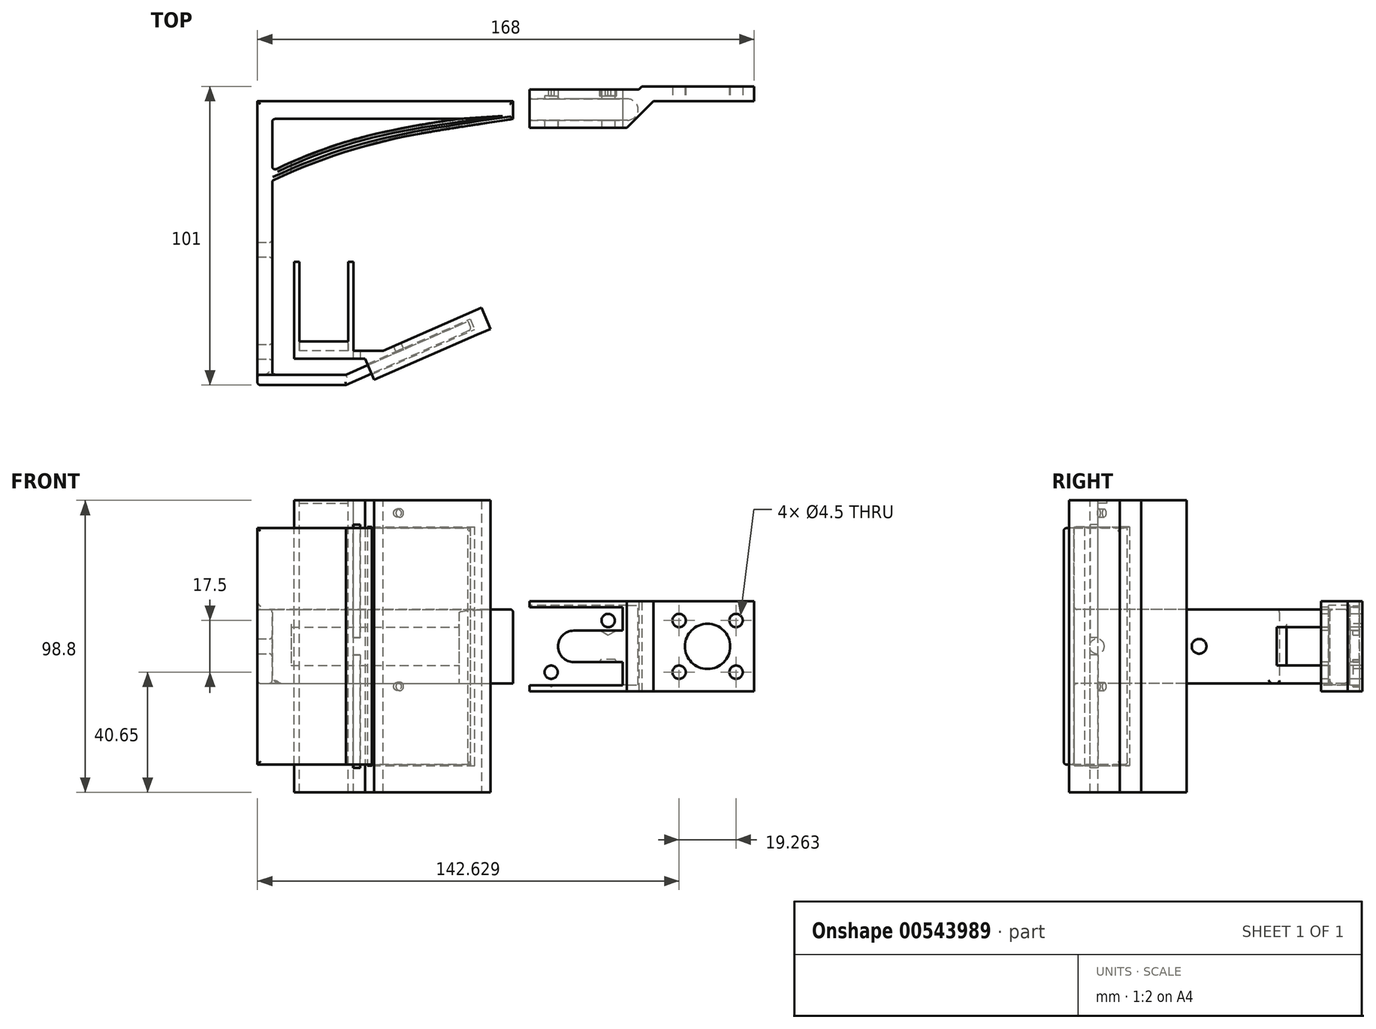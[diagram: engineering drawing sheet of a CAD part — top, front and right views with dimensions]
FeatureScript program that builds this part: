
annotation { "Feature Type Name" : "Feature", "Feature Type Description" : "" }
export const myFeature = defineFeature(function(context is Context, id is Id, definition is map)
    precondition{}
    {
        {
            var Q0;
            Q0=qCreatedBy(makeId("Top.planeOp"),FACE);
            var sketch = newSketch(context, id + "F0", { "sketchPlane" : qUnion([Q0])});
            skLineSegment(sketch, "E0.bottom", {"start": v(-68.2, 34.46) * mm, "end": v(54.8, 34.46) * mm});
            skLineSegment(sketch, "E0.left", {"start": v(-68.2, 34.46) * mm, "end": v(-68.2, 28.46) * mm});
            skLineSegment(sketch, "E1.bottom", {"start": v(-68.2, 28.46) * mm, "end": v(-63.2, 28.46) * mm});
            skLineSegment(sketch, "E1.top", {"start": v(-68.2, -61.54) * mm, "end": v(-63.2, -61.54) * mm});
            skLineSegment(sketch, "E1.left", {"start": v(-68.2, 28.46) * mm, "end": v(-68.2, -61.54) * mm});
            skLineSegment(sketch, "E2", {"start": v(-63.2, 7.6) * mm, "end": v(-63.2, -61.54) * mm});
            skLineSegment(sketch, "E3", {"start": v(-63.2, 28.46) * mm, "end": v(-63.2, 10.83) * mm});
            skFitSpline(sketch, "E4", {"points": [v(-63.2, 10.83) * mm, v(-36.5, 21.22) * mm, v(0, 28.46) * mm], "startDerivative": vector(52.11, 25.6) * mm, "endDerivative": vector(73.7, 10.1) * mm});
            skFitSpline(sketch, "E5", {"points": [v(-63.2, 7.6) * mm, v(-25.3, 20.96) * mm, v(18.24, 28.46) * mm], "startDerivative": vector(89.55, 42.22) * mm, "endDerivative": vector(130.6, 19.81) * mm});
            skLineSegment(sketch, "E6", {"start": v(54.8, 34.46) * mm, "end": v(54.8, 32.96) * mm});
            skLineSegment(sketch, "E7", {"start": v(54.8, 29.96) * mm, "end": v(54.8, 28.46) * mm});
            skLineSegment(sketch, "E8", {"start": v(18.24, 28.46) * mm, "end": v(54.8, 28.46) * mm});
            skLineSegment(sketch, "E9", {"start": v(-63.2, 28.46) * mm, "end": v(0, 28.46) * mm});
            skLineSegment(sketch, "E10", {"start": v(54.8, 32.96) * mm, "end": v(54.8, 29.96) * mm});
            skSolve(sketch);
        }
        {
            var Q0;
            Q0=makeQuery(id+"F0.imprint","IMPRINT",FACE,{"disambiguationData":[TD([[makeQuery(id+"F0.imprint","IMPRINT",EDGE,{"derivedFrom":sQuery(id+"F0.wireOp",EDGE,"E0.bottom")}),-1.0]])]});
            extrude(context, id + "F1", {"entities" : qUnion([Q0]), "depth" : 25 * mm, "offsetDistance" : 25 * mm});
        }
        {
            var Q0;
            Q0=makeQuery(id+"F1.opExtrude","SWEPT_FACE",FACE,{"disambiguationData":[OSD([sQuery(id+"F0.wireOp",EDGE,"E2")])]});
            var sketch = newSketch(context, id + "F2", { "sketchPlane" : qUnion([Q0])});
            skCircle(sketch, "E11", {"center": v(-50.3, 12.5) * mm, "radius": 2.5 * mm});
            skCircle(sketch, "E12", {"center": v(-15.75, 12.5) * mm, "radius": 2.5 * mm});
            skSolve(sketch);
        }
        {
            var Q0;
            Q0=makeQuery(id+"F2.imprint","IMPRINT",FACE,{"disambiguationData":[TD([[makeQuery(id+"F2.imprint","IMPRINT",EDGE,{"derivedFrom":sQuery(id+"F2.wireOp",EDGE,"E12")}),1.0]])]});
            var Q1;
            Q1=makeQuery(id+"F2.imprint","IMPRINT",FACE,{"disambiguationData":[TD([[makeQuery(id+"F2.imprint","IMPRINT",EDGE,{"derivedFrom":sQuery(id+"F2.wireOp",EDGE,"E11")}),1.0]])]});
            extrude(context, id + "F3", {"entities" : qUnion([Q0, Q1]), "operationType" : NewBodyOperationType.REMOVE, "endBound" : BoundingType.THROUGH_ALL, "oppositeDirection" : true, "depth" : 25 * mm, "offsetDistance" : 25 * mm});
        }
        {
            var Q0;
            Q0=makeQuery(id+"F1.opExtrude","SWEPT_FACE",FACE,{"disambiguationData":[OSD([sQuery(id+"F0.wireOp",EDGE,"E9")])]});
            var sketch = newSketch(context, id + "F4", { "sketchPlane" : qUnion([Q0])});
            skLineSegment(sketch, "E13.bottom", {"start": v(0, 6.04) * mm, "end": v(-56.85, 6.04) * mm});
            skLineSegment(sketch, "E13.top", {"start": v(0, 18.96) * mm, "end": v(-56.85, 18.96) * mm});
            skLineSegment(sketch, "E13.left", {"start": v(0, 6.04) * mm, "end": v(0, 18.96) * mm});
            skLineSegment(sketch, "E13.right", {"start": v(-56.85, 6.04) * mm, "end": v(-56.85, 18.96) * mm});
            skLineSegment(sketch, "E14.0", {"start": v(-63.2, 25) * mm, "end": v(0, 25) * mm});
            skLineSegment(sketch, "E15.0", {"start": v(-63.2, 0) * mm, "end": v(0, 0) * mm});
            skLineSegment(sketch, "E16", {"start": v(0, 25) * mm, "end": v(0, 18.96) * mm});
            skLineSegment(sketch, "E17", {"start": v(0, 6.04) * mm, "end": v(0, 0) * mm});
            skSolve(sketch);
        }
        {
            var Q0;
            Q0=makeQuery(id+"F4.imprint","IMPRINT",FACE,{"disambiguationData":[TD([[makeQuery(id+"F4.imprint","IMPRINT",EDGE,{"derivedFrom":sQuery(id+"F4.wireOp",EDGE,"E13.bottom")}),-1.0]])]});
            extrude(context, id + "F5", {"entities" : qUnion([Q0]), "operationType" : NewBodyOperationType.REMOVE, "endBound" : BoundingType.THROUGH_ALL, "depth" : 25 * mm, "offsetDistance" : 25 * mm});
        }
        {
            var Q0;
            Q0=makeQuery(id+"F1.opExtrude","SWEPT_FACE",FACE,{"disambiguationData":[OSD([sQuery(id+"F0.wireOp",EDGE,"E8")])]});
            var sketch = newSketch(context, id + "F6", { "sketchPlane" : qUnion([Q0])});
            skLineSegment(sketch, "E18", {"start": v(54.8, 25) * mm, "end": v(54.8, 18.5) * mm});
            skLineSegment(sketch, "E19", {"start": v(54.8, 18.5) * mm, "end": v(54.8, 6.5) * mm});
            skLineSegment(sketch, "E20", {"start": v(54.8, 6.5) * mm, "end": v(54.8, 0) * mm});
            skLineSegment(sketch, "E21", {"start": v(54.8, 18.5) * mm, "end": v(38.8, 18.5) * mm});
            skLineSegment(sketch, "E22", {"start": v(32.8, 12.5) * mm, "end": v(32.8, 12.5) * mm});
            skLineSegment(sketch, "E23", {"start": v(38.8, 6.5) * mm, "end": v(54.8, 6.5) * mm});
            skPoint(sketch, "E24.visualSharp", {"position": v(32.8, 18.5) * mm});
            skArc(sketch, "E24.filletArc", {"start": v(38.8, 18.5) * mm, "mid": v(34.55, 16.74) * mm, "end": v(32.8, 12.5) * mm});
            skPoint(sketch, "E25.visualSharp", {"position": v(32.8, 6.5) * mm});
            skArc(sketch, "E25.filletArc", {"start": v(32.8, 12.5) * mm, "mid": v(34.55, 8.26) * mm, "end": v(38.8, 6.5) * mm});
            skCircle(sketch, "E26", {"center": v(31.16, 21.25) * mm, "radius": 2.25 * mm});
            skCircle(sketch, "E27.MirrorC", {"center": v(31.16, 3.75) * mm, "radius": 2.25 * mm});
            skCircle(sketch, "E28.MirrorC", {"center": v(50.42, 21.25) * mm, "radius": 2.25 * mm});
            skCircle(sketch, "E29.MirrorC", {"center": v(50.42, 3.75) * mm, "radius": 2.25 * mm});
            skSolve(sketch);
        }
        {
            var Q0;
            Q0=makeQuery(id+"F6.imprint","IMPRINT",FACE,{"disambiguationData":[TD([[makeQuery(id+"F6.imprint","IMPRINT",EDGE,{"derivedFrom":sQuery(id+"F6.wireOp",EDGE,"E26")}),1.0]])]});
            var Q1;
            Q1=makeQuery(id+"F6.imprint","IMPRINT",FACE,{"disambiguationData":[TD([[makeQuery(id+"F6.imprint","IMPRINT",EDGE,{"derivedFrom":sQuery(id+"F6.wireOp",EDGE,"E28.MirrorC")}),-1.0]])]});
            var Q2;
            Q2=makeQuery(id+"F6.imprint","IMPRINT",FACE,{"disambiguationData":[TD([[makeQuery(id+"F6.imprint","IMPRINT",EDGE,{"derivedFrom":sQuery(id+"F6.wireOp",EDGE,"E19")}),-1.0]])]});
            var Q3;
            Q3=makeQuery(id+"F6.imprint","IMPRINT",FACE,{"disambiguationData":[TD([[makeQuery(id+"F6.imprint","IMPRINT",EDGE,{"derivedFrom":sQuery(id+"F6.wireOp",EDGE,"E29.MirrorC")}),1.0]])]});
            var Q4;
            Q4=makeQuery(id+"F6.imprint","IMPRINT",FACE,{"disambiguationData":[TD([[makeQuery(id+"F6.imprint","IMPRINT",EDGE,{"derivedFrom":sQuery(id+"F6.wireOp",EDGE,"E27.MirrorC")}),-1.0]])]});
            extrude(context, id + "F7", {"entities" : qUnion([Q0, Q1, Q2, Q3, Q4]), "operationType" : NewBodyOperationType.REMOVE, "oppositeDirection" : true, "depth" : 25 * mm, "offsetDistance" : 25 * mm});
        }
        {
            var Q0;
            Q0=makeQuery(id+"F1.opExtrude","SWEPT_FACE",FACE,{"disambiguationData":[OSD([sQuery(id+"F0.wireOp",EDGE,"E1.top")])]});
            var sketch = newSketch(context, id + "F8", { "sketchPlane" : qUnion([Q0])});
            skLineSegment(sketch, "E30.bottom", {"start": v(-68.2, 12.5) * mm, "end": v(-38.2, 12.5) * mm});
            skLineSegment(sketch, "E30.top", {"start": v(-68.2, -27.5) * mm, "end": v(-38.2, -27.5) * mm});
            skLineSegment(sketch, "E30.left", {"start": v(-68.2, 12.5) * mm, "end": v(-68.2, -27.5) * mm});
            skLineSegment(sketch, "E30.right", {"start": v(-38.2, 12.5) * mm, "end": v(-38.2, -27.5) * mm});
            skLineSegment(sketch, "E31.top", {"start": v(-68.2, 52.5) * mm, "end": v(-38.2, 52.5) * mm});
            skLineSegment(sketch, "E31.left", {"start": v(-68.2, 12.5) * mm, "end": v(-68.2, 52.5) * mm});
            skLineSegment(sketch, "E31.right", {"start": v(-38.2, 12.5) * mm, "end": v(-38.2, 52.5) * mm});
            skSolve(sketch);
        }
        {
            var Q0;
            {var subQ4=sQuery(id+"F8.wireOp",EDGE,"E31.top");Q0=makeQuery(id+"F8.imprint","IMPRINT",FACE,{"disambiguationData":[TD([[makeQuery(id+"F8.imprint","IMPRINT",EDGE,{"derivedFrom":subQ4}),-1.0]])]});}
            var Q1;
            {var subQ4=sQuery(id+"F8.wireOp",EDGE,"E30.top");Q1=makeQuery(id+"F8.imprint","IMPRINT",FACE,{"disambiguationData":[TD([[makeQuery(id+"F8.imprint","IMPRINT",EDGE,{"derivedFrom":subQ4}),1.0]])]});}
            extrude(context, id + "F9", {"entities" : qUnion([Q0, Q1]), "operationType" : NewBodyOperationType.ADD, "oppositeDirection" : true, "depth" : 3.5 * mm, "offsetDistance" : 25 * mm});
        }
        {
            var Q0;
            Q0=makeQuery(id+"F9.opExtrude","SWEPT_FACE",FACE,{"disambiguationData":[OSD([sQuery(id+"F8.wireOp",EDGE,"E31.top")])]});
            var sketch = newSketch(context, id + "F10", { "sketchPlane" : qUnion([Q0])});
            skLineSegment(sketch, "E32", {"start": v(-38.2, -58.04) * mm, "end": v(3.02, -40) * mm});
            skLineSegment(sketch, "E33", {"start": v(3.02, -40) * mm, "end": v(4.22, -42.75) * mm});
            skLineSegment(sketch, "E34", {"start": v(4.22, -42.75) * mm, "end": v(-38.2, -61.54) * mm});
            skSolve(sketch);
        }
        {
            var Q0;
            Q0=makeQuery(id+"F10.imprint","IMPRINT",FACE,{"disambiguationData":[TD([[makeQuery(id+"F10.imprint","IMPRINT",EDGE,{"derivedFrom":sQuery(id+"F10.wireOp",EDGE,"E32")}),-1.0]])]});
            extrude(context, id + "F11", {"entities" : qUnion([Q0]), "operationType" : NewBodyOperationType.ADD, "oppositeDirection" : true, "depth" : 80 * mm, "offsetDistance" : 25 * mm});
        }
        {
            var Q0;
            Q0=makeQuery(id+"F1.opExtrude","CAP_EDGE",EDGE,{"disambiguationData":[OSD([sQuery(id+"F0.wireOp",EDGE,"E0.bottom")])],"isStart":false});
            var Q1;
            Q1=makeQuery(id+"F1.opExtrude","CAP_EDGE",EDGE,{"disambiguationData":[OSD([sQuery(id+"F0.wireOp",EDGE,"E0.bottom")])],"isStart":true});
            var Q2;
            {var subQ0=sQuery(id+"F0.wireOp",EDGE,"E0.bottom");var subQ3=sQuery(id+"F0.wireOp",EDGE,"E6");Q2=makeQuery(id+"F7.boolean.opBoolean","SPLIT",EDGE,{"disambiguationData":[TD([makeQuery(id+"F7.opExtrude","SWEPT_FACE",FACE,{"disambiguationData":[OSD([sQuery(id+"F6.wireOp",EDGE,"E21")])]})])],"derivedFrom":makeQuery(id+"F1.opExtrude","SWEPT_EDGE",EDGE,{"disambiguationData":[OSD([subQ0,subQ3])]})});}
            var Q3;
            {var subQ2=sQuery(id+"F0.wireOp",EDGE,"E10");var subQ3=sQuery(id+"F0.wireOp",EDGE,"E7");var subQ4=sQuery(id+"F0.wireOp",EDGE,"E6");Q3=makeQuery(id+"F7.boolean.opBoolean","SPLIT",FACE,{"disambiguationData":[TD([makeQuery(id+"F7.opExtrude","SWEPT_FACE",FACE,{"disambiguationData":[OSD([sQuery(id+"F6.wireOp",EDGE,"E21")])]})])],"derivedFrom":makeQuery(id+"F1.opExtrude","SWEPT_FACE",FACE,{"disambiguationData":[OSD([subQ4,subQ3,subQ2])]})});}
            var Q4;
            Q4=makeQuery(id+"F7.boolean.opBoolean","COPY",EDGE,{"derivedFrom":makeQuery(id+"F7.opExtrude","SWEPT_EDGE",EDGE,{"disambiguationData":[OSD([sQuery(id+"F6.wireOp",EDGE,"E18"),sQuery(id+"F6.wireOp",EDGE,"E19"),sQuery(id+"F6.wireOp",EDGE,"E21")])]})});
            var Q5;
            Q5=makeQuery(id+"F7.boolean.opBoolean","COPY",EDGE,{"derivedFrom":makeQuery(id+"F7.opExtrude","SWEPT_EDGE",EDGE,{"disambiguationData":[OSD([sQuery(id+"F6.wireOp",EDGE,"E19"),sQuery(id+"F6.wireOp",EDGE,"E20"),sQuery(id+"F6.wireOp",EDGE,"E23")])]})});
            var Q6;
            Q6=makeQuery(id+"F7.boolean.opBoolean","INTERSECT",EDGE,{"derivedFrom":[makeQuery(id+"F1.opExtrude","SWEPT_FACE",FACE,{"disambiguationData":[OSD([sQuery(id+"F0.wireOp",EDGE,"E0.bottom")])]}),makeQuery(id+"F7.opExtrude","SWEPT_FACE",FACE,{"disambiguationData":[OSD([sQuery(id+"F6.wireOp",EDGE,"E23")])]})]});
            var Q7;
            Q7=makeQuery(id+"F7.boolean.opBoolean","INTERSECT",EDGE,{"derivedFrom":[makeQuery(id+"F1.opExtrude","SWEPT_FACE",FACE,{"disambiguationData":[OSD([sQuery(id+"F0.wireOp",EDGE,"E0.bottom")])]}),makeQuery(id+"F7.opExtrude","SWEPT_FACE",FACE,{"disambiguationData":[OSD([sQuery(id+"F6.wireOp",EDGE,"E24.filletArc"),sQuery(id+"F6.wireOp",EDGE,"E25.filletArc")])]})]});
            var Q8;
            {var subQ1=sQuery(id+"F0.wireOp",EDGE,"E8");var subQ2=sQuery(id+"F0.wireOp",EDGE,"E7");Q8=makeQuery(id+"F7.boolean.opBoolean","SPLIT",EDGE,{"disambiguationData":[TD([makeQuery(id+"F7.opExtrude","SWEPT_FACE",FACE,{"disambiguationData":[OSD([sQuery(id+"F6.wireOp",EDGE,"E23")])]})])],"derivedFrom":makeQuery(id+"F1.opExtrude","SWEPT_EDGE",EDGE,{"disambiguationData":[OSD([subQ2,subQ1])]})});}
            var Q9;
            Q9=makeQuery(id+"F1.opExtrude","CAP_EDGE",EDGE,{"disambiguationData":[OSD([sQuery(id+"F0.wireOp",EDGE,"E8")])],"isStart":true});
            var Q10;
            Q10=makeQuery(id+"F1.opExtrude","SWEPT_FACE",FACE,{"disambiguationData":[OSD([sQuery(id+"F0.wireOp",EDGE,"E2")])]});
            var Q11;
            Q11=makeQuery(id+"F1.opExtrude","CAP_EDGE",EDGE,{"disambiguationData":[OSD([sQuery(id+"F0.wireOp",EDGE,"E0.left"),sQuery(id+"F0.wireOp",EDGE,"E1.left")])],"isStart":true});
            var Q12;
            Q12=makeQuery(id+"F1.opExtrude","SWEPT_FACE",FACE,{"disambiguationData":[OSD([sQuery(id+"F0.wireOp",EDGE,"E3")])]});
            var Q13;
            Q13=makeQuery(id+"F11.opExtrude","CAP_EDGE",EDGE,{"disambiguationData":[OSD([sQuery(id+"F10.wireOp",EDGE,"E32")])],"isStart":false});
            var Q14;
            Q14=makeQuery(id+"F11.opExtrude","CAP_EDGE",EDGE,{"disambiguationData":[OSD([sQuery(id+"F10.wireOp",EDGE,"E34")])],"isStart":false});
            var Q15;
            Q15=makeQuery(id+"F9.opExtrude","CAP_EDGE",EDGE,{"disambiguationData":[OSD([sQuery(id+"F8.wireOp",EDGE,"E30.top")])],"isStart":false});
            var Q16;
            Q16=makeQuery(id+"F9.opExtrude","CAP_EDGE",EDGE,{"disambiguationData":[OSD([sQuery(id+"F8.wireOp",EDGE,"E30.top")])],"isStart":true});
            var Q17;
            Q17=makeQuery(id+"F11.opExtrude","SWEPT_EDGE",EDGE,{"disambiguationData":[OSD([sQuery(id+"F10.wireOp",EDGE,"E33"),sQuery(id+"F10.wireOp",EDGE,"E34")])]});
            var Q18;
            Q18=makeQuery(id+"F11.opExtrude","CAP_EDGE",EDGE,{"disambiguationData":[OSD([sQuery(id+"F10.wireOp",EDGE,"E34")])],"isStart":true});
            var Q19;
            Q19=makeQuery(id+"F9.opExtrude","CAP_EDGE",EDGE,{"disambiguationData":[OSD([sQuery(id+"F8.wireOp",EDGE,"E31.top")])],"isStart":true});
            var Q20;
            Q20=makeQuery(id+"F9.boolean.opBoolean","MERGE",EDGE,{"derivedFrom":[makeQuery(id+"F1.opExtrude","SWEPT_EDGE",EDGE,{"disambiguationData":[OSD([sQuery(id+"F0.wireOp",EDGE,"E1.top"),sQuery(id+"F0.wireOp",EDGE,"E1.left")])]}),makeQuery(id+"F9.opExtrude","CAP_EDGE",EDGE,{"disambiguationData":[OSD([sQuery(id+"F8.wireOp",EDGE,"E30.left")])],"isStart":true}),makeQuery(id+"F9.opExtrude","CAP_EDGE",EDGE,{"disambiguationData":[OSD([sQuery(id+"F8.wireOp",EDGE,"E31.left")])],"isStart":true})]});
            var Q21;
            Q21=makeQuery(id+"F1.opExtrude","CAP_FACE",FACE,{"disambiguationData":[OSD([sQuery(id+"F0.wireOp",EDGE,"E0.bottom"),sQuery(id+"F0.wireOp",EDGE,"E0.left"),sQuery(id+"F0.wireOp",EDGE,"E1.top"),sQuery(id+"F0.wireOp",EDGE,"E1.left"),sQuery(id+"F0.wireOp",EDGE,"E2"),sQuery(id+"F0.wireOp",EDGE,"E3"),sQuery(id+"F0.wireOp",EDGE,"E4"),sQuery(id+"F0.wireOp",EDGE,"E5"),sQuery(id+"F0.wireOp",EDGE,"E6"),sQuery(id+"F0.wireOp",EDGE,"E7"),sQuery(id+"F0.wireOp",EDGE,"E8"),sQuery(id+"F0.wireOp",EDGE,"E9"),sQuery(id+"F0.wireOp",EDGE,"E10")])],"isStart":false});
            var Q22;
            Q22=makeQuery(id+"F5.boolean.opBoolean","INTERSECT",EDGE,{"derivedFrom":[makeQuery(id+"F1.opExtrude","SWEPT_FACE",FACE,{"disambiguationData":[OSD([sQuery(id+"F0.wireOp",EDGE,"E4")])]}),makeQuery(id+"F5.opExtrude","SWEPT_FACE",FACE,{"disambiguationData":[OSD([sQuery(id+"F4.wireOp",EDGE,"E13.top")])]})]});
            fillet(context, id + "F12", {"entities" : qUnion([Q0, Q1, Q2, Q3, Q4, Q5, Q6, Q7, Q8, Q9, Q10, Q11, Q12, Q13, Q14, Q15, Q16, Q17, Q18, Q19, Q20, Q21, Q22]), "radius" : 1 * mm, "tangentPropagation" : true, "allowEdgeOverflow" : false});
        }
        {
            var Q0;
            Q0=makeQuery(id+"F1.opExtrude","SWEPT_FACE",FACE,{"disambiguationData":[OSD([sQuery(id+"F0.wireOp",EDGE,"E0.bottom")])]});
            var sketch = newSketch(context, id + "F13", { "sketchPlane" : qUnion([Q0])});
            skCircle(sketch, "E35.0", {"center": v(-31.16, 3.75) * mm, "radius": 2.25 * mm});
            skCircle(sketch, "E35.1", {"center": v(-31.16, 21.25) * mm, "radius": 2.25 * mm});
            skArc(sketch, "E35.2", {"start": v(-51.84, 19.5) * mm, "mid": v(-50.42, 23.5) * mm, "end": v(-49, 19.5) * mm});
            skArc(sketch, "E35.3", {"start": v(-49, 19.5) * mm, "mid": v(-50.42, 19) * mm, "end": v(-51.84, 19.5) * mm});
            skArc(sketch, "E35.4", {"start": v(-51.84, 5.5) * mm, "mid": v(-50.42, 6) * mm, "end": v(-49, 5.5) * mm});
            skArc(sketch, "E35.5", {"start": v(-51.84, 5.5) * mm, "mid": v(-50.42, 1.5) * mm, "end": v(-49, 5.5) * mm});
            skLineSegment(sketch, "E36.0", {"start": v(-54.8, 5.5) * mm, "end": v(-54.8, 1) * mm});
            skLineSegment(sketch, "E36.1", {"start": v(-54.8, 19.5) * mm, "end": v(-54.8, 24) * mm});
            skLineSegment(sketch, "E37.0", {"start": v(-55.4, 19.5) * mm, "end": v(-55.4, 24) * mm});
            skLineSegment(sketch, "E38.0", {"start": v(-55.4, 5.5) * mm, "end": v(-55.4, 1) * mm});
            skLineSegment(sketch, "E39.0", {"start": v(-38.8, 18.5) * mm, "end": v(-53.8, 18.5) * mm});
            skLineSegment(sketch, "E39.1", {"start": v(-53.8, 6.5) * mm, "end": v(-38.8, 6.5) * mm});
            skLineSegment(sketch, "E40.0", {"start": v(-53.8, 7.2) * mm, "end": v(-38.8, 7.2) * mm});
            skLineSegment(sketch, "E41.0", {"start": v(-38.8, 17.8) * mm, "end": v(-53.8, 17.8) * mm});
            skLineSegment(sketch, "E42", {"start": v(-53.8, 17.8) * mm, "end": v(-55.4, 17.8) * mm});
            skLineSegment(sketch, "E43", {"start": v(-55.4, 17.8) * mm, "end": v(-55.4, 19.5) * mm});
            skLineSegment(sketch, "E44", {"start": v(-53.8, 7.2) * mm, "end": v(-55.4, 7.2) * mm});
            skLineSegment(sketch, "E45", {"start": v(-55.4, 7.2) * mm, "end": v(-55.4, 5.5) * mm});
            skLineSegment(sketch, "E46.0", {"start": v(-53.8, 25) * mm, "end": v(67.2, 25) * mm});
            skLineSegment(sketch, "E46.1", {"start": v(67.2, 0) * mm, "end": v(-54.8, 0) * mm});
            skLineSegment(sketch, "E47.0", {"start": v(-53.8, 25.7) * mm, "end": v(67.2, 25.7) * mm});
            skLineSegment(sketch, "E48.0", {"start": v(67.2, -0.7) * mm, "end": v(-54.8, -0.7) * mm});
            skLineSegment(sketch, "E49", {"start": v(-55.4, 1) * mm, "end": v(-55.4, -0.7) * mm});
            skLineSegment(sketch, "E50", {"start": v(-55.4, -0.7) * mm, "end": v(-54.8, -0.7) * mm});
            skLineSegment(sketch, "E51", {"start": v(-55.4, 24) * mm, "end": v(-55.4, 25.7) * mm});
            skLineSegment(sketch, "E52", {"start": v(-55.4, 25.7) * mm, "end": v(-53.8, 25.7) * mm});
            skArc(sketch, "E53.0", {"start": v(-38.8, 6.5) * mm, "mid": v(-32.8, 12.5) * mm, "end": v(-38.8, 18.5) * mm});
            skArc(sketch, "E54.0", {"start": v(-38.8, 7.2) * mm, "mid": v(-33.5, 12.5) * mm, "end": v(-38.8, 17.8) * mm});
            skLineSegment(sketch, "E55", {"start": v(-23.79, 25.7) * mm, "end": v(-23.79, -0.7) * mm});
            skLineSegment(sketch, "E56", {"start": v(-23.79, -0.7) * mm, "end": v(-23.79, -2.7) * mm});
            skLineSegment(sketch, "E57", {"start": v(-23.79, -2.7) * mm, "end": v(-99.79, -2.7) * mm});
            skLineSegment(sketch, "E58", {"start": v(-23.79, 25.7) * mm, "end": v(-23.79, 27.7) * mm});
            skLineSegment(sketch, "E59", {"start": v(-23.79, 27.7) * mm, "end": v(-99.79, 27.7) * mm});
            skLineSegment(sketch, "E60", {"start": v(-99.79, 27.7) * mm, "end": v(-99.79, -2.7) * mm});
            skCircle(sketch, "E61.0", {"center": v(-74.42, 3.75) * mm, "radius": 2.25 * mm});
            skCircle(sketch, "E61.1", {"center": v(-74.42, 21.25) * mm, "radius": 2.25 * mm});
            skArc(sketch, "E61.2", {"start": v(-95.1, 19.5) * mm, "mid": v(-93.68, 23.5) * mm, "end": v(-92.27, 19.5) * mm});
            skArc(sketch, "E61.3", {"start": v(-92.27, 19.5) * mm, "mid": v(-93.68, 19) * mm, "end": v(-95.1, 19.5) * mm});
            skArc(sketch, "E61.4", {"start": v(-95.1, 5.5) * mm, "mid": v(-93.68, 6) * mm, "end": v(-92.27, 5.5) * mm});
            skArc(sketch, "E61.5", {"start": v(-95.1, 5.5) * mm, "mid": v(-93.68, 1.5) * mm, "end": v(-92.27, 5.5) * mm});
            skLineSegment(sketch, "E62", {"start": v(-61.79, 27.7) * mm, "end": v(-61.79, -2.7) * mm});
            skLineSegment(sketch, "E63", {"start": v(-74.42, 21.25) * mm, "end": v(-93.68, 3.75) * mm});
            skCircle(sketch, "E64", {"center": v(-84.05, 12.5) * mm, "radius": 7.65 * mm});
            skSolve(sketch);
        }
        {
            var Q0;
            Q0=makeQuery(id+"F13.imprint","IMPRINT",FACE,{"disambiguationData":[TD([[makeQuery(id+"F13.imprint","IMPRINT",EDGE,{"derivedFrom":sQuery(id+"F13.wireOp",EDGE,"E37.0")}),1.0]])]});
            var Q1;
            Q1=makeQuery(id+"F13.imprint","IMPRINT",FACE,{"disambiguationData":[TD([[makeQuery(id+"F13.imprint","IMPRINT",EDGE,{"derivedFrom":sQuery(id+"F13.wireOp",EDGE,"E35.0")}),1.0]])]});
            var Q2;
            Q2=makeQuery(id+"F13.imprint","IMPRINT",FACE,{"disambiguationData":[TD([[makeQuery(id+"F13.imprint","IMPRINT",EDGE,{"derivedFrom":sQuery(id+"F13.wireOp",EDGE,"E35.3")}),1.0]])]});
            extrude(context, id + "F14", {"entities" : qUnion([Q0, Q1, Q2]), "depth" : 4 * mm, "offsetDistance" : 25 * mm, "hasSecondDirection" : true, "secondDirectionOppositeDirection" : true, "secondDirectionDepth" : 9 * mm});
        }
        {
            var Q0;
            {var subQ3=sQuery(id+"F13.wireOp",EDGE,"E60");Q0=makeQuery(id+"F13.imprint","IMPRINT",FACE,{"disambiguationData":[TD([[makeQuery(id+"F13.imprint","IMPRINT",EDGE,{"derivedFrom":subQ3}),1.0]])]});}
            extrude(context, id + "F15", {"entities" : qUnion([Q0]), "operationType" : NewBodyOperationType.ADD, "depth" : 5 * mm, "offsetDistance" : 25 * mm});
        }
        {
            var Q0;
            Q0=makeQuery(id+"F14.opExtrude","SWEPT_FACE",FACE,{"disambiguationData":[OSD([sQuery(id+"F13.wireOp",EDGE,"E55"),sQuery(id+"F13.wireOp",EDGE,"E56"),sQuery(id+"F13.wireOp",EDGE,"E58")])]});
            var sketch = newSketch(context, id + "F16", { "sketchPlane" : qUnion([Q0])});
            skLineSegment(sketch, "E65.bottom", {"start": v(-35.23, -0.57) * mm, "end": v(-28.05, -0.57) * mm});
            skLineSegment(sketch, "E65.top", {"start": v(-35.23, 26.43) * mm, "end": v(-28.05, 26.43) * mm});
            skLineSegment(sketch, "E65.left", {"start": v(-35.23, -0.57) * mm, "end": v(-35.23, 26.43) * mm});
            skLineSegment(sketch, "E65.right", {"start": v(-28.05, -0.57) * mm, "end": v(-28.05, 26.43) * mm});
            skSolve(sketch);
        }
        {
            var Q0;
            Q0=makeQuery(id+"F16.imprint","IMPRINT",FACE,{"disambiguationData":[TD([[makeQuery(id+"F16.imprint","IMPRINT",EDGE,{"derivedFrom":sQuery(id+"F16.wireOp",EDGE,"E65.bottom")}),1.0]])]});
            extrude(context, id + "F17", {"entities" : qUnion([Q0]), "operationType" : NewBodyOperationType.REMOVE, "oppositeDirection" : true, "depth" : 33.2 * mm, "offsetDistance" : 25 * mm});
        }
        {
            var Q0;
            Q0=makeQuery(id+"F14.opExtrude","CAP_EDGE",EDGE,{"disambiguationData":[OSD([sQuery(id+"F13.wireOp",EDGE,"E62")])],"isStart":true});
            chamfer(context, id + "F18", {"entities" : qUnion([Q0]), "width" : 5 * mm, "tangentPropagation" : true});
        }
        {
            var Q0;
            {var subQ0=sQuery(id+"F13.wireOp",EDGE,"E57");Q0=makeQuery(id+"F15.boolean.opBoolean","MERGE",FACE,{"derivedFrom":[makeQuery(id+"F14.opExtrude","SWEPT_FACE",FACE,{"disambiguationData":[OSD([subQ0])]}),makeQuery(id+"F15.opExtrude","SWEPT_FACE",FACE,{"disambiguationData":[OSD([subQ0])]})]});}
            var sketch = newSketch(context, id + "F19", { "sketchPlane" : qUnion([Q0])});
            skLineSegment(sketch, "E66", {"start": v(61.79, -30.46) * mm, "end": v(65.79, -34.46) * mm});
            skLineSegment(sketch, "E67", {"start": v(61.79, -39.46) * mm, "end": v(60.79, -38.46) * mm});
            skSolve(sketch);
        }
        {
            var Q0;
            {var subQ0=sQuery(id+"F19.wireOp",EDGE,"E66");Q0=makeQuery(id+"F19.imprint","IMPRINT",FACE,{"disambiguationData":[TD([[makeQuery(id+"F19.imprint","IMPRINT",EDGE,{"derivedFrom":subQ0}),-1.0]])]});}
            var Q1;
            {var subQ0=sQuery(id+"F19.wireOp",EDGE,"E67");Q1=makeQuery(id+"F19.imprint","IMPRINT",FACE,{"disambiguationData":[TD([[makeQuery(id+"F19.imprint","IMPRINT",EDGE,{"derivedFrom":subQ0}),-1.0]])]});}
            var Q2;
            {var subQ0=sQuery(id+"F13.wireOp",EDGE,"E59");Q2=makeQuery(id+"F15.boolean.opBoolean","MERGE",FACE,{"derivedFrom":[makeQuery(id+"F14.opExtrude","SWEPT_FACE",FACE,{"disambiguationData":[OSD([subQ0])]}),makeQuery(id+"F15.opExtrude","SWEPT_FACE",FACE,{"disambiguationData":[OSD([subQ0])]})]});}
            extrude(context, id + "F20", {"entities" : qUnion([Q0, Q1]), "operationType" : NewBodyOperationType.ADD, "endBound" : BoundingType.UP_TO_SURFACE, "oppositeDirection" : true, "depth" : 25 * mm, "endBoundEntityFace" : qUnion([Q2]), "offsetDistance" : 25 * mm});
        }
        {
            var Q0;
            Q0=makeQuery(id+"F14.opExtrude","CAP_FACE",FACE,{"disambiguationData":[OSD([sQuery(id+"F13.wireOp",EDGE,"E35.0"),sQuery(id+"F13.wireOp",EDGE,"E35.1"),sQuery(id+"F13.wireOp",EDGE,"E35.2"),sQuery(id+"F13.wireOp",EDGE,"E35.3"),sQuery(id+"F13.wireOp",EDGE,"E35.4"),sQuery(id+"F13.wireOp",EDGE,"E35.5"),sQuery(id+"F13.wireOp",EDGE,"E55"),sQuery(id+"F13.wireOp",EDGE,"E56"),sQuery(id+"F13.wireOp",EDGE,"E57"),sQuery(id+"F13.wireOp",EDGE,"E58"),sQuery(id+"F13.wireOp",EDGE,"E59"),sQuery(id+"F13.wireOp",EDGE,"E62")])],"isStart":false});
            var sketch = newSketch(context, id + "F21", { "sketchPlane" : qUnion([Q0])});
            skCircle(sketch, "E68.cCircle", {"center": v(-50.42, 3.75) * mm, "radius": 4.3 * mm, "construction": true});
            skLineSegment(sketch, "E68.0", {"start": v(-55.39, 3.85) * mm, "end": v(-52.82, 8.1) * mm});
            skLineSegment(sketch, "E68.1", {"start": v(-52.82, 8.1) * mm, "end": v(-47.85, 8) * mm});
            skLineSegment(sketch, "E68.2", {"start": v(-47.85, 8) * mm, "end": v(-45.46, 3.65) * mm});
            skLineSegment(sketch, "E68.3", {"start": v(-45.46, 3.65) * mm, "end": v(-48.03, -0.6) * mm});
            skLineSegment(sketch, "E68.4", {"start": v(-48.03, -0.6) * mm, "end": v(-53, -0.5) * mm});
            skLineSegment(sketch, "E68.5", {"start": v(-53, -0.5) * mm, "end": v(-55.39, 3.85) * mm});
            skPoint(sketch, "E68.0.midPoint", {"position": v(-54.1, 5.97) * mm});
            skCircle(sketch, "E69.cCircle", {"center": v(-50.42, 21.25) * mm, "radius": 4.3 * mm, "construction": true});
            skLineSegment(sketch, "E69.0", {"start": v(-54.72, 18.77) * mm, "end": v(-54.72, 23.73) * mm});
            skLineSegment(sketch, "E69.1", {"start": v(-54.72, 23.73) * mm, "end": v(-50.42, 26.22) * mm});
            skLineSegment(sketch, "E69.2", {"start": v(-50.42, 26.22) * mm, "end": v(-46.12, 23.73) * mm});
            skLineSegment(sketch, "E69.3", {"start": v(-46.12, 23.73) * mm, "end": v(-46.12, 18.77) * mm});
            skLineSegment(sketch, "E69.4", {"start": v(-46.12, 18.77) * mm, "end": v(-50.42, 16.28) * mm});
            skLineSegment(sketch, "E69.5", {"start": v(-50.42, 16.28) * mm, "end": v(-54.72, 18.77) * mm});
            skPoint(sketch, "E69.0.midPoint", {"position": v(-54.72, 21.25) * mm});
            skCircle(sketch, "E70.cCircle", {"center": v(-31.16, 21.25) * mm, "radius": 4.3 * mm, "construction": true});
            skLineSegment(sketch, "E70.0", {"start": v(-35.46, 18.77) * mm, "end": v(-35.46, 23.73) * mm});
            skLineSegment(sketch, "E70.1", {"start": v(-35.46, 23.73) * mm, "end": v(-31.16, 26.22) * mm});
            skLineSegment(sketch, "E70.2", {"start": v(-31.16, 26.22) * mm, "end": v(-26.86, 23.73) * mm});
            skLineSegment(sketch, "E70.3", {"start": v(-26.86, 23.73) * mm, "end": v(-26.86, 18.77) * mm});
            skLineSegment(sketch, "E70.4", {"start": v(-26.86, 18.77) * mm, "end": v(-31.16, 16.28) * mm});
            skLineSegment(sketch, "E70.5", {"start": v(-31.16, 16.28) * mm, "end": v(-35.46, 18.77) * mm});
            skPoint(sketch, "E70.0.midPoint", {"position": v(-35.46, 21.25) * mm});
            skCircle(sketch, "E71.cCircle", {"center": v(-31.16, 3.75) * mm, "radius": 4.3 * mm, "construction": true});
            skLineSegment(sketch, "E71.0", {"start": v(-35.46, 1.27) * mm, "end": v(-35.46, 6.23) * mm});
            skLineSegment(sketch, "E71.1", {"start": v(-35.46, 6.23) * mm, "end": v(-31.16, 8.72) * mm});
            skLineSegment(sketch, "E71.2", {"start": v(-31.16, 8.72) * mm, "end": v(-26.86, 6.23) * mm});
            skLineSegment(sketch, "E71.3", {"start": v(-26.86, 6.23) * mm, "end": v(-26.86, 1.27) * mm});
            skLineSegment(sketch, "E71.4", {"start": v(-26.86, 1.27) * mm, "end": v(-31.16, -1.22) * mm});
            skLineSegment(sketch, "E71.5", {"start": v(-31.16, -1.22) * mm, "end": v(-35.46, 1.27) * mm});
            skPoint(sketch, "E71.0.midPoint", {"position": v(-35.46, 3.75) * mm});
            skSolve(sketch);
        }
        {
            var Q0;
            Q0=makeQuery(id+"F21.imprint","IMPRINT",FACE,{"disambiguationData":[TD([[makeQuery(id+"F21.imprint","IMPRINT",EDGE,{"derivedFrom":sQuery(id+"F21.wireOp",EDGE,"E69.0")}),-1.0]])]});
            var Q1;
            Q1=makeQuery(id+"F21.imprint","IMPRINT",FACE,{"disambiguationData":[TD([[makeQuery(id+"F21.imprint","IMPRINT",EDGE,{"derivedFrom":sQuery(id+"F21.wireOp",EDGE,"E70.0")}),-1.0]])]});
            var Q2;
            Q2=makeQuery(id+"F21.imprint","IMPRINT",FACE,{"disambiguationData":[TD([[makeQuery(id+"F21.imprint","IMPRINT",EDGE,{"derivedFrom":sQuery(id+"F21.wireOp",EDGE,"E71.0")}),-1.0]])]});
            var Q3;
            Q3=makeQuery(id+"F21.imprint","IMPRINT",FACE,{"disambiguationData":[TD([[makeQuery(id+"F21.imprint","IMPRINT",EDGE,{"derivedFrom":sQuery(id+"F21.wireOp",EDGE,"E68.0")}),-1.0]])]});
            extrude(context, id + "F22", {"entities" : qUnion([Q0, Q1, Q2, Q3]), "operationType" : NewBodyOperationType.REMOVE, "oppositeDirection" : true, "depth" : 2.2 * mm, "offsetDistance" : 25 * mm});
        }
        {
            var Q0;
            Q0=makeQuery(id+"F17.boolean.opBoolean","COPY",FACE,{"derivedFrom":makeQuery(id+"F17.opExtrude","SWEPT_FACE",FACE,{"disambiguationData":[OSD([sQuery(id+"F16.wireOp",EDGE,"E65.top")])]})});
            var sketch = newSketch(context, id + "F23", { "sketchPlane" : qUnion([Q0])});
            skLineSegment(sketch, "E72.0", {"start": v(56.99, -35.23) * mm, "end": v(56.99, -28.05) * mm});
            skArc(sketch, "E73", {"start": v(56.99, -35.23) * mm, "mid": v(60.58, -31.64) * mm, "end": v(56.99, -28.05) * mm});
            skSolve(sketch);
        }
        {
            var Q0;
            Q0=makeQuery(id+"F23.imprint","IMPRINT",FACE,{"disambiguationData":[TD([[makeQuery(id+"F23.imprint","IMPRINT",EDGE,{"derivedFrom":sQuery(id+"F23.wireOp",EDGE,"E72.0")}),-1.0]])]});
            var Q1;
            Q1=makeQuery(id+"F17.boolean.opBoolean","COPY",FACE,{"derivedFrom":makeQuery(id+"F17.opExtrude","SWEPT_FACE",FACE,{"disambiguationData":[OSD([sQuery(id+"F16.wireOp",EDGE,"E65.bottom")])]})});
            extrude(context, id + "F24", {"entities" : qUnion([Q0]), "operationType" : NewBodyOperationType.REMOVE, "endBound" : BoundingType.UP_TO_SURFACE, "depth" : 25 * mm, "endBoundEntityFace" : qUnion([Q1]), "offsetDistance" : 25 * mm});
        }
        {
            var Q0;
            Q0=makeQuery(id+"F11.opExtrude","SWEPT_FACE",FACE,{"disambiguationData":[OSD([sQuery(id+"F10.wireOp",EDGE,"E33")])]});
            cPlane(context, id + "F25", {"entities" : qUnion([Q0]), "cplaneType" : CPlaneType.OFFSET, "offset" : 0 * mm, "width" : 150 * mm, "height" : 150 * mm});
        }
        {
            var Q0;
            Q0=qCreatedBy(id+"F25.planeOp",FACE);
            var sketch = newSketch(context, id + "F26", { "sketchPlane" : qUnion([Q0])});
            skLineSegment(sketch, "E74.0", {"start": v(-38.86, -27.5) * mm, "end": v(-39.86, -27.5) * mm});
            skLineSegment(sketch, "E75.0", {"start": v(-37.86, -26.5) * mm, "end": v(-37.86, 52.5) * mm});
            skLineSegment(sketch, "E76.0", {"start": v(-40.86, -26.5) * mm, "end": v(-40.86, 51.5) * mm});
            skLineSegment(sketch, "E77.0", {"start": v(-37.46, -26.5) * mm, "end": v(-37.46, 52.5) * mm});
            skLineSegment(sketch, "E78.0", {"start": v(-41.26, -26.5) * mm, "end": v(-41.26, 51.5) * mm});
            skLineSegment(sketch, "E79.0", {"start": v(-37.86, 52.9) * mm, "end": v(-39.86, 52.9) * mm});
            skLineSegment(sketch, "E80.0", {"start": v(-38.86, -27.9) * mm, "end": v(-39.86, -27.9) * mm});
            skLineSegment(sketch, "E81", {"start": v(-41.26, 51.5) * mm, "end": v(-41.26, 52.9) * mm});
            skLineSegment(sketch, "E82", {"start": v(-41.26, 52.9) * mm, "end": v(-39.86, 52.9) * mm});
            skLineSegment(sketch, "E83", {"start": v(-37.86, 52.9) * mm, "end": v(-37.46, 52.9) * mm});
            skLineSegment(sketch, "E84", {"start": v(-37.46, 52.9) * mm, "end": v(-37.46, 52.5) * mm});
            skLineSegment(sketch, "E85", {"start": v(-37.46, -26.5) * mm, "end": v(-37.46, -27.9) * mm});
            skLineSegment(sketch, "E86", {"start": v(-37.46, -27.9) * mm, "end": v(-38.86, -27.9) * mm});
            skLineSegment(sketch, "E87", {"start": v(-39.86, -27.9) * mm, "end": v(-41.26, -27.9) * mm});
            skLineSegment(sketch, "E88", {"start": v(-41.26, -27.9) * mm, "end": v(-41.26, -26.5) * mm});
            skLineSegment(sketch, "E89.bottom", {"start": v(-35.46, 61.9) * mm, "end": v(-43.26, 61.9) * mm});
            skLineSegment(sketch, "E89.top", {"start": v(-35.46, -36.9) * mm, "end": v(-43.26, -36.9) * mm});
            skLineSegment(sketch, "E89.left", {"start": v(-35.46, 61.9) * mm, "end": v(-35.46, -36.9) * mm});
            skLineSegment(sketch, "E89.right", {"start": v(-43.26, 61.9) * mm, "end": v(-43.26, -36.9) * mm});
            skSolve(sketch);
        }
        {
            var Q0;
            Q0=makeQuery(id+"F26.imprint","IMPRINT",FACE,{"disambiguationData":[TD([[makeQuery(id+"F26.imprint","IMPRINT",EDGE,{"derivedFrom":sQuery(id+"F26.wireOp",EDGE,"E77.0")}),-1.0]])]});
            extrude(context, id + "F27", {"entities" : qUnion([Q0]), "oppositeDirection" : true, "depth" : 37 * mm, "offsetDistance" : 25 * mm, "hasSecondDirection" : true, "secondDirectionOppositeDirection" : false, "secondDirectionDepth" : 1 * mm});
        }
        {
            var Q0;
            Q0=makeQuery(id+"F27.opExtrude","SWEPT_FACE",FACE,{"disambiguationData":[OSD([sQuery(id+"F26.wireOp",EDGE,"E89.top")])]});
            var sketch = newSketch(context, id + "F28", { "sketchPlane" : qUnion([Q0])});
            skLineSegment(sketch, "E90.0", {"start": v(-31.84, 52.63) * mm, "end": v(-28.71, 59.78) * mm});
            skLineSegment(sketch, "E91.bottom", {"start": v(-61.9, -20.28) * mm, "end": v(58.1, -20.28) * mm});
            skLineSegment(sketch, "E91.top", {"start": v(-61.9, 99.72) * mm, "end": v(58.1, 99.72) * mm});
            skLineSegment(sketch, "E91.left", {"start": v(-61.9, -20.28) * mm, "end": v(-61.9, 99.72) * mm});
            skLineSegment(sketch, "E91.right", {"start": v(58.1, -20.28) * mm, "end": v(58.1, 99.72) * mm});
            skCircle(sketch, "E92", {"center": v(-53.64, 91.47) * mm, "radius": 2.75 * mm});
            skLineSegment(sketch, "E93.0", {"start": v(-31.84, 52.63) * mm, "end": v(2.97, 37.4) * mm});
            skLineSegment(sketch, "E94.0", {"start": v(2.97, 37.4) * mm, "end": v(6.1, 44.55) * mm});
            skLineSegment(sketch, "E95.0", {"start": v(-28.71, 59.78) * mm, "end": v(6.1, 44.55) * mm});
            skLineSegment(sketch, "E96", {"start": v(2.97, 37.4) * mm, "end": v(7.55, 35.4) * mm});
            skLineSegment(sketch, "E97", {"start": v(7.55, 35.4) * mm, "end": v(10.7, 42.57) * mm});
            skLineSegment(sketch, "E98", {"start": v(6.1, 44.55) * mm, "end": v(10.7, 42.57) * mm});
            skPoint(sketch, "E99.startSnap0", {"position": v(-30.28, 56.2) * mm});
            skCircle(sketch, "E100", {"center": v(-53.64, -12.03) * mm, "radius": 2.75 * mm});
            skCircle(sketch, "E101", {"center": v(49.86, 91.47) * mm, "radius": 2.75 * mm});
            skSolve(sketch);
        }
        {
            var Q0;
            Q0=makeQuery(id+"F28.imprint","IMPRINT",FACE,{"disambiguationData":[TD([[makeQuery(id+"F28.imprint","IMPRINT",EDGE,{"derivedFrom":sQuery(id+"F28.wireOp",EDGE,"E94.0")}),-1.0]])]});
            var Q1;
            Q1=makeQuery(id+"F27.opExtrude","SWEPT_FACE",FACE,{"disambiguationData":[OSD([sQuery(id+"F26.wireOp",EDGE,"E89.bottom")])]});
            extrude(context, id + "F29", {"entities" : qUnion([Q0]), "operationType" : NewBodyOperationType.ADD, "endBound" : BoundingType.UP_TO_SURFACE, "oppositeDirection" : true, "depth" : 25 * mm, "endBoundEntityFace" : qUnion([Q1]), "offsetDistance" : 25 * mm});
        }
        {
            var Q0;
            {var subQ0=sQuery(id+"F26.wireOp",EDGE,"E89.bottom");Q0=makeQuery(id+"F29.boolean.opBoolean","MERGE",FACE,{"derivedFrom":[makeQuery(id+"F27.opExtrude","SWEPT_FACE",FACE,{"disambiguationData":[OSD([subQ0])]}),makeQuery(id+"F29.opExtrude","CAP_FACE",FACE,{"disambiguationData":[OSD([subQ0])],"isStart":false})]});}
            var sketch = newSketch(context, id + "F30", { "sketchPlane" : qUnion([Q0])});
            skLineSegment(sketch, "E102", {"start": v(-31.84, -52.63) * mm, "end": v(-55.84, -52.63) * mm});
            skLineSegment(sketch, "E103", {"start": v(-55.84, -52.63) * mm, "end": v(-55.84, -49.93) * mm});
            skLineSegment(sketch, "E104", {"start": v(-55.84, -49.93) * mm, "end": v(-25.67, -49.93) * mm});
            skLineSegment(sketch, "E105", {"start": v(-55.84, -49.93) * mm, "end": v(-55.84, -19.93) * mm});
            skLineSegment(sketch, "E106", {"start": v(-55.84, -19.93) * mm, "end": v(-54.04, -19.93) * mm});
            skLineSegment(sketch, "E107", {"start": v(-54.04, -19.93) * mm, "end": v(-54.04, -49.93) * mm});
            skLineSegment(sketch, "E108", {"start": v(-54.04, -49.93) * mm, "end": v(-37.54, -49.93) * mm});
            skLineSegment(sketch, "E109", {"start": v(-37.54, -49.93) * mm, "end": v(-37.54, -19.93) * mm});
            skLineSegment(sketch, "E110", {"start": v(-37.54, -19.93) * mm, "end": v(-35.74, -19.93) * mm});
            skLineSegment(sketch, "E111", {"start": v(-35.74, -19.93) * mm, "end": v(-35.74, -49.93) * mm});
            skLineSegment(sketch, "E112", {"start": v(-31.84, -52.63) * mm, "end": v(-25.67, -49.93) * mm});
            skSolve(sketch);
        }
        {
            var Q0;
            {var subQ4=sQuery(id+"F30.wireOp",EDGE,"E102");Q0=makeQuery(id+"F30.imprint","IMPRINT",FACE,{"disambiguationData":[TD([[makeQuery(id+"F30.imprint","IMPRINT",EDGE,{"derivedFrom":subQ4}),-1.0]])]});}
            var Q1;
            {var subQ0=sQuery(id+"F30.wireOp",EDGE,"E109");Q1=makeQuery(id+"F30.imprint","IMPRINT",FACE,{"disambiguationData":[TD([[makeQuery(id+"F30.imprint","IMPRINT",EDGE,{"derivedFrom":subQ0}),-1.0]])]});}
            var Q2;
            {var subQ0=sQuery(id+"F30.wireOp",EDGE,"E105");Q2=makeQuery(id+"F30.imprint","IMPRINT",FACE,{"disambiguationData":[TD([[makeQuery(id+"F30.imprint","IMPRINT",EDGE,{"derivedFrom":subQ0}),-1.0]])]});}
            var Q3;
            Q3=makeQuery(id+"F29.boolean.opBoolean","MERGE",FACE,{"derivedFrom":[makeQuery(id+"F27.opExtrude","SWEPT_FACE",FACE,{"disambiguationData":[OSD([sQuery(id+"F26.wireOp",EDGE,"E89.top")])]}),makeQuery(id+"F29.opExtrude","CAP_FACE",FACE,{"disambiguationData":[OSD([sQuery(id+"F28.wireOp",EDGE,"E94.0"),sQuery(id+"F28.wireOp",EDGE,"E96"),sQuery(id+"F28.wireOp",EDGE,"E97"),sQuery(id+"F28.wireOp",EDGE,"E98")])],"isStart":true})]});
            extrude(context, id + "F31", {"entities" : qUnion([Q0, Q1, Q2]), "operationType" : NewBodyOperationType.ADD, "endBound" : BoundingType.UP_TO_SURFACE, "oppositeDirection" : true, "depth" : 25 * mm, "endBoundEntityFace" : qUnion([Q3]), "offsetDistance" : 25 * mm});
        }
        {
            var Q0;
            Q0=makeQuery(id+"F31.opExtrude","SWEPT_FACE",FACE,{"disambiguationData":[OSD([sQuery(id+"F30.wireOp",EDGE,"E102")])]});
            var sketch = newSketch(context, id + "F32", { "sketchPlane" : qUnion([Q0])});
            skLineSegment(sketch, "E113.bottom", {"start": v(-33.39, 53.65) * mm, "end": v(-35.79, 53.65) * mm});
            skLineSegment(sketch, "E113.top", {"start": v(-33.39, 15.43) * mm, "end": v(-35.79, 15.43) * mm});
            skLineSegment(sketch, "E113.left", {"start": v(-33.39, 53.65) * mm, "end": v(-33.39, 15.43) * mm});
            skLineSegment(sketch, "E113.right", {"start": v(-35.79, 53.65) * mm, "end": v(-35.79, 15.43) * mm});
            skLineSegment(sketch, "E114", {"start": v(-55.84, 12.5) * mm, "end": v(-31.84, 12.5) * mm});
            skLineSegment(sketch, "E115.MirrorCS", {"start": v(-35.79, -28.65) * mm, "end": v(-35.79, 9.57) * mm});
            skLineSegment(sketch, "E116.MirrorCS", {"start": v(-33.39, 9.57) * mm, "end": v(-35.79, 9.57) * mm});
            skLineSegment(sketch, "E117.MirrorCS", {"start": v(-33.39, -28.65) * mm, "end": v(-33.39, 9.57) * mm});
            skLineSegment(sketch, "E118.MirrorCS", {"start": v(-33.39, -28.65) * mm, "end": v(-35.79, -28.65) * mm});
            skSolve(sketch);
        }
        {
            var Q0;
            Q0=makeQuery(id+"F32.imprint","IMPRINT",FACE,{"disambiguationData":[TD([[makeQuery(id+"F32.imprint","IMPRINT",EDGE,{"derivedFrom":sQuery(id+"F32.wireOp",EDGE,"E113.bottom")}),1.0]])]});
            var Q1;
            Q1=makeQuery(id+"F32.imprint","IMPRINT",FACE,{"disambiguationData":[TD([[makeQuery(id+"F32.imprint","IMPRINT",EDGE,{"derivedFrom":sQuery(id+"F32.wireOp",EDGE,"E115.MirrorCS")}),-1.0]])]});
            var Q2;
            Q2=makeQuery(id+"F31.opExtrude","SWEPT_FACE",FACE,{"disambiguationData":[OSD([sQuery(id+"F30.wireOp",EDGE,"E104")])]});
            extrude(context, id + "F33", {"entities" : qUnion([Q0, Q1]), "operationType" : NewBodyOperationType.REMOVE, "endBound" : BoundingType.UP_TO_SURFACE, "oppositeDirection" : true, "depth" : 25 * mm, "endBoundEntityFace" : qUnion([Q2]), "offsetDistance" : 25 * mm});
        }
        {
            var Q0;
            Q0=makeQuery(id+"F29.boolean.opBoolean","MERGE",FACE,{"derivedFrom":[makeQuery(id+"F27.opExtrude","SWEPT_FACE",FACE,{"disambiguationData":[OSD([sQuery(id+"F26.wireOp",EDGE,"E89.left")])]}),makeQuery(id+"F29.opExtrude","SWEPT_FACE",FACE,{"disambiguationData":[OSD([sQuery(id+"F28.wireOp",EDGE,"E96")])]})]});
            var sketch = newSketch(context, id + "F34", { "sketchPlane" : qUnion([Q0])});
            skCircle(sketch, "E119", {"center": v(38.27, 57.6) * mm, "radius": 1.4 * mm});
            skCircle(sketch, "E120", {"center": v(38.27, -1.05) * mm, "radius": 1.4 * mm});
            skLineSegment(sketch, "E121", {"start": v(38.27, -1.05) * mm, "end": v(38.27, 32.76) * mm});
            skSolve(sketch);
        }
        {
            var Q0;
            Q0=makeQuery(id+"F34.imprint","IMPRINT",FACE,{"disambiguationData":[TD([[makeQuery(id+"F34.imprint","IMPRINT",EDGE,{"derivedFrom":sQuery(id+"F34.wireOp",EDGE,"E119")}),1.0]])]});
            var Q1;
            Q1=makeQuery(id+"F34.imprint","IMPRINT",FACE,{"disambiguationData":[TD([[makeQuery(id+"F34.imprint","IMPRINT",EDGE,{"derivedFrom":sQuery(id+"F34.wireOp",EDGE,"E120")}),1.0]])]});
            var Q2;
            Q2=makeQuery(id+"F27.opExtrude","SWEPT_FACE",FACE,{"disambiguationData":[OSD([sQuery(id+"F26.wireOp",EDGE,"E77.0"),sQuery(id+"F26.wireOp",EDGE,"E84"),sQuery(id+"F26.wireOp",EDGE,"E85")])]});
            extrude(context, id + "F35", {"entities" : qUnion([Q0, Q1]), "operationType" : NewBodyOperationType.REMOVE, "endBound" : BoundingType.UP_TO_SURFACE, "oppositeDirection" : true, "depth" : 5 * mm, "endBoundEntityFace" : qUnion([Q2]), "offsetDistance" : 25 * mm});
        }
        {
            var Q0;
            {var subQ0=sQuery(id+"F26.wireOp",EDGE,"E89.bottom");Q0=makeQuery(id+"F31.boolean.opBoolean","MERGE",FACE,{"derivedFrom":[makeQuery(id+"F29.boolean.opBoolean","MERGE",FACE,{"derivedFrom":[makeQuery(id+"F27.opExtrude","SWEPT_FACE",FACE,{"disambiguationData":[OSD([subQ0])]}),makeQuery(id+"F29.opExtrude","CAP_FACE",FACE,{"disambiguationData":[OSD([subQ0])],"isStart":false})]}),makeQuery(id+"F31.opExtrude","CAP_FACE",FACE,{"disambiguationData":[OSD([sQuery(id+"F30.wireOp",EDGE,"E102"),sQuery(id+"F30.wireOp",EDGE,"E103"),sQuery(id+"F30.wireOp",EDGE,"E104"),sQuery(id+"F30.wireOp",EDGE,"E105"),sQuery(id+"F30.wireOp",EDGE,"E106"),sQuery(id+"F30.wireOp",EDGE,"E107"),sQuery(id+"F30.wireOp",EDGE,"E108"),sQuery(id+"F30.wireOp",EDGE,"E109"),sQuery(id+"F30.wireOp",EDGE,"E110"),sQuery(id+"F30.wireOp",EDGE,"E111"),sQuery(id+"F30.wireOp",EDGE,"E112")])],"isStart":true})]});}
            var sketch = newSketch(context, id + "F36", { "sketchPlane" : qUnion([Q0])});
            skLineSegment(sketch, "E122", {"start": v(-54.04, -46.83) * mm, "end": v(-37.54, -46.83) * mm});
            skSolve(sketch);
        }
        {
            var Q0;
            {var subQ0=sQuery(id+"F36.wireOp",EDGE,"E122");Q0=makeQuery(id+"F36.imprint","IMPRINT",FACE,{"disambiguationData":[TD([[makeQuery(id+"F36.imprint","IMPRINT",EDGE,{"derivedFrom":subQ0}),-1.0]])]});}
            extrude(context, id + "F37", {"entities" : qUnion([Q0]), "operationType" : NewBodyOperationType.ADD, "oppositeDirection" : true, "depth" : 1 * mm, "offsetDistance" : 25 * mm});
        }
    });
